# Revit family: HL_RU_Roof drain_HL64.1BH-B-221103
name_source: partatom
category: Sanitärinstallationen
units: mm (PartAtom-declared; Revit-internal decimal feet)

## family parameters
Arbeitsebenenbasiert = Nein
Beim Laden mit Abzugskörper schneiden = Nein
Bemaßung runder Anschluss = Durchmesser verwenden
Gemeinsam genutzt = Nein
Immer vertikal = Ja
OmniClass-Nummer = 23.70.50.21.24.14
OmniClass-Titel = Deck Waste Water Drains
Raumberechnungspunkt = Ja
Teiletyp = Normal

## types (1)
- HL_Кровельная воронка_HL64.1BH
    Abwasserrohrverbindung = Ja
    Bauelement = HL64.1BH
    Beschreibung = Кровельные воронки
    EAN = 9003076864126
    HW-Verbindung = Nein
    Hersteller = HL Hutterer & Lechner GmbH
    KW-Verbindung = Nein
    Lüftungsverbindung = Nein
    Modell = HL64.1BH
    Typenkommentare = HL64.1BH Кровельная воронка DN75/110 горизонтальный с битумным полотном и подогревом (10_30Вт/230В). Проходная _ 148х148мм/137х137мм.,
    URL = http://www.hutterer-lechner.com
    Vorgabe-Ansicht = 0 mm  [stored 0 ft]
    ВЕС = 2,44 [kg]
    ВЫСОТА МОНТАЖА = 167 mm
    МАКСИМАЛЬНАЯ НАГРУЗКА КЛАССА = K - 300 kg
    МАТЕРИАЛ = PP
    НАСАДКА = 12-65mm/148x148mm
    ПРОИЗВОДИТЕЛЬНОСТЬ = 3,7 l/s
    РАЗМЕР = DN75/110
    РЕШЁТКА = Edelstahl 137x137mm

note: [stored X ft] marks values corroborated as IEEE doubles in the binary element streams (Revit-internal decimal feet)

## geometry (parser evidence)
native form markers: Sweep x10
no freeform markers — native parametric forms only
